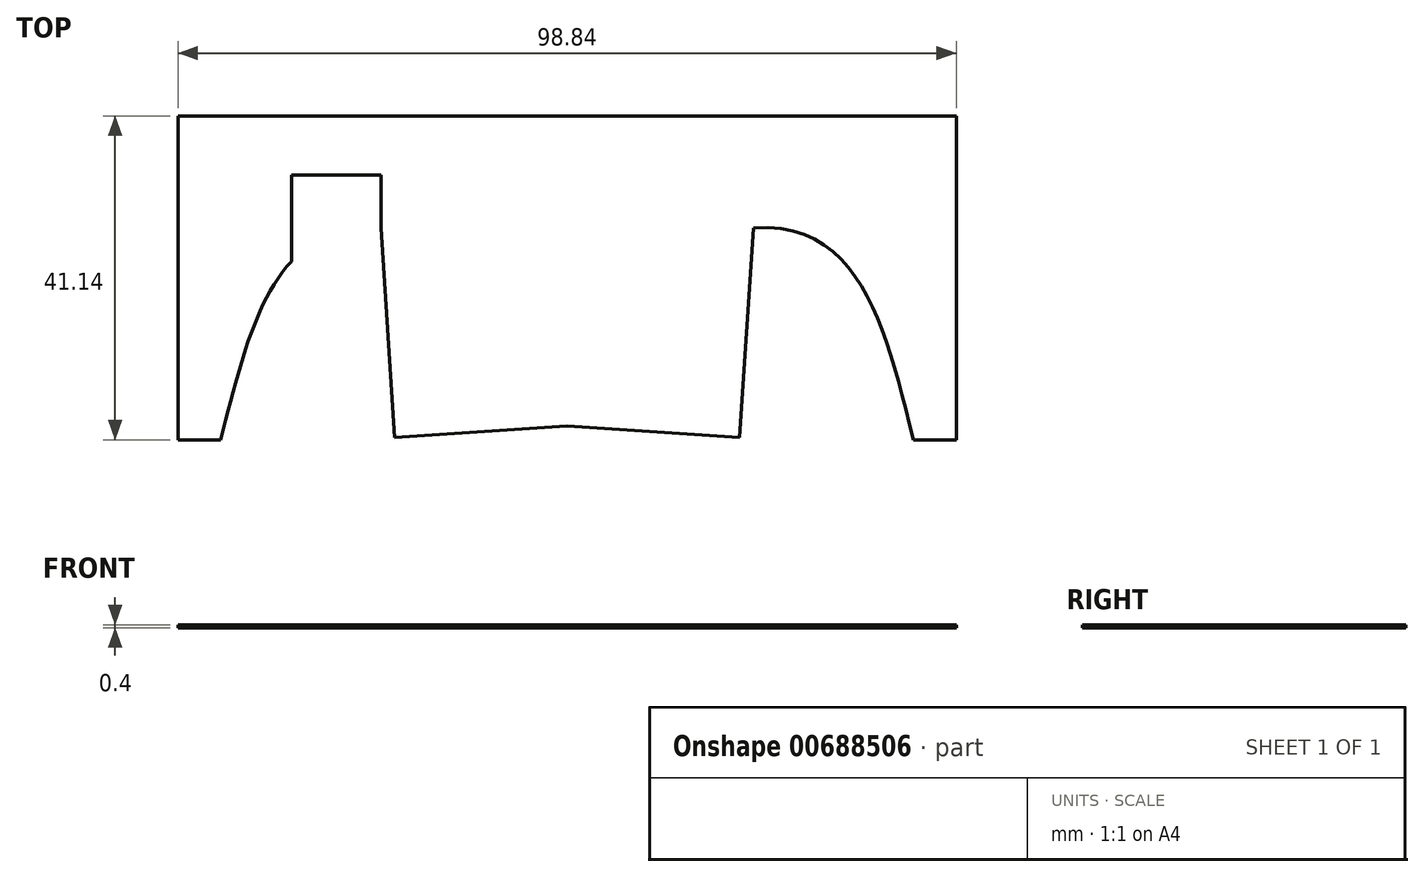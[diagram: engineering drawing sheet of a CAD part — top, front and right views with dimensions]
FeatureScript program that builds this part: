
annotation { "Feature Type Name" : "Feature", "Feature Type Description" : "" }
export const myFeature = defineFeature(function(context is Context, id is Id, definition is map)
    precondition{}
    {
        {
            var Q0;
            Q0=qCreatedBy(makeId("Top.planeOp"),FACE);
            var sketch = newSketch(context, id + "F0", { "sketchPlane" : qUnion([Q0])});
            skLineSegment(sketch, "E0", {"start": v(23.67, -12.67) * mm, "end": v(21.9, -39.28) * mm});
            skLineSegment(sketch, "E1", {"start": v(44, -39.58) * mm, "end": v(49.42, -39.58) * mm});
            skLineSegment(sketch, "E2", {"start": v(49.42, -39.58) * mm, "end": v(49.42, 1.56) * mm});
            skLineSegment(sketch, "E3", {"start": v(49.42, 1.56) * mm, "end": v(0, 1.56) * mm});
            skLineSegment(sketch, "E4", {"start": v(21.9, -39.28) * mm, "end": v(0, -37.83) * mm});
            skLineSegment(sketch, "E5", {"start": v(0, 1.56) * mm, "end": v(0, -37.83) * mm});
            skFitSpline(sketch, "E6", {"points": [v(44, -39.58) * mm, v(36.93, -19.39) * mm, v(23.67, -12.67) * mm], "startDerivative": vector(-11.55, 45.48) * mm, "endDerivative": vector(-43.32, -3.51) * mm});
            skLineSegment(sketch, "E7.MirrorCS", {"start": v(-21.9, -39.28) * mm, "end": v(0, -37.83) * mm});
            skLineSegment(sketch, "E8.MirrorCS", {"start": v(-23.67, -12.67) * mm, "end": v(-21.9, -39.28) * mm});
            skLineSegment(sketch, "E9.MirrorCS", {"start": v(-44, -39.58) * mm, "end": v(-49.42, -39.58) * mm});
            skLineSegment(sketch, "E10.MirrorCS", {"start": v(-49.42, 1.56) * mm, "end": v(0, 1.56) * mm});
            skLineSegment(sketch, "E11.MirrorCS", {"start": v(-49.42, -39.58) * mm, "end": v(-49.42, 1.56) * mm});
            skFitSpline(sketch, "E12.MirrorCS", {"points": [v(-44, -39.58) * mm, v(-36.93, -19.39) * mm, v(-23.67, -12.67) * mm], "startDerivative": vector(11.55, 45.48) * mm, "endDerivative": vector(43.32, -3.51) * mm});
            skLineSegment(sketch, "E13.bottom", {"start": v(-35.03, -5.94) * mm, "end": v(-23.67, -5.94) * mm});
            skLineSegment(sketch, "E13.top", {"start": v(-35.03, -19.9) * mm, "end": v(-23.67, -17.15) * mm});
            skLineSegment(sketch, "E13.left", {"start": v(-35.03, -5.94) * mm, "end": v(-35.03, -19.9) * mm});
            skLineSegment(sketch, "E13.right", {"start": v(-23.67, -5.94) * mm, "end": v(-23.67, -17.15) * mm});
            skSolve(sketch);
        }
        {
            var Q0;
            Q0=makeQuery(id+"F0.imprint","IMPRINT",FACE,{"disambiguationData":[TD([[makeQuery(id+"F0.imprint","IMPRINT",EDGE,{"derivedFrom":sQuery(id+"F0.wireOp",EDGE,"E5")}),-1.0]])]});
            var Q1;
            Q1=makeQuery(id+"F0.imprint","IMPRINT",FACE,{"disambiguationData":[TD([[makeQuery(id+"F0.imprint","IMPRINT",EDGE,{"derivedFrom":sQuery(id+"F0.wireOp",EDGE,"E0")}),-1.0]])]});
            extrude(context, id + "F1", {"entities" : qUnion([Q0, Q1]), "depth" : 0.4 * mm, "offsetDistance" : 25 * mm});
        }
    });
